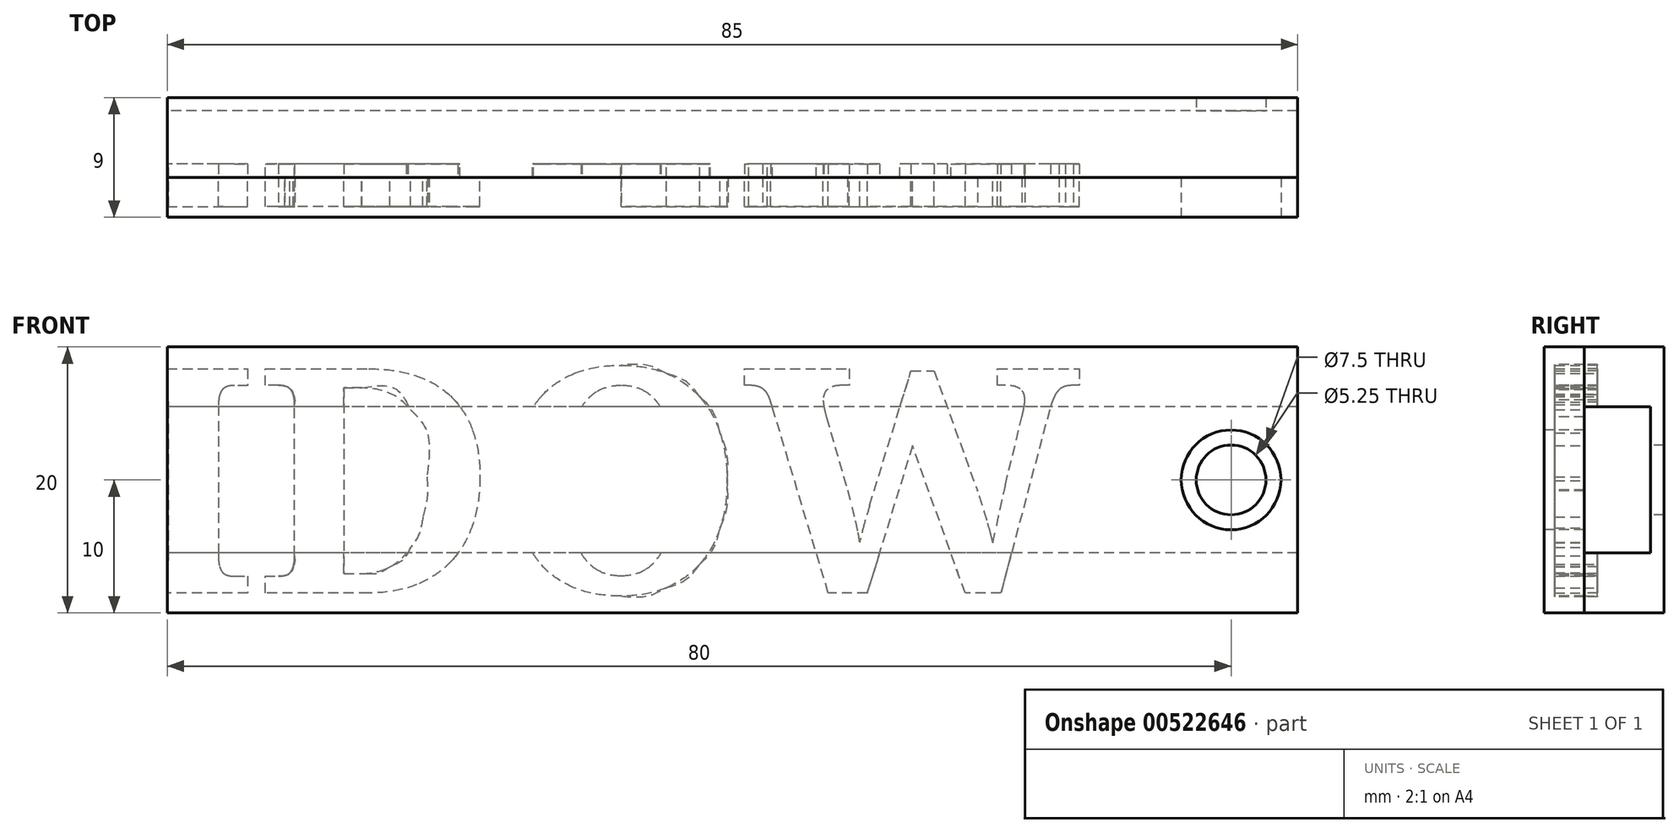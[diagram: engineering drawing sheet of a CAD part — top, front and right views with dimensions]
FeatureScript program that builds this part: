
annotation { "Feature Type Name" : "Feature", "Feature Type Description" : "" }
export const myFeature = defineFeature(function(context is Context, id is Id, definition is map)
    precondition{}
    {
        {
            var Q0;
            Q0=qCreatedBy(makeId("Front.planeOp"),FACE);
            var sketch = newSketch(context, id + "F0", { "sketchPlane" : qUnion([Q0])});
            skLineSegment(sketch, "E0.bottom", {"start": v(105, 10) * mm, "end": v(-105, 10) * mm});
            skLineSegment(sketch, "E0.top", {"start": v(105, -10) * mm, "end": v(-105, -10) * mm});
            skLineSegment(sketch, "E0.left", {"start": v(105, 10) * mm, "end": v(105, -10) * mm});
            skLineSegment(sketch, "E0.right", {"start": v(-105, 10) * mm, "end": v(-105, -10) * mm});
            skPoint(sketch, "E0.middle", {"position": v(0, 0) * mm});
            skSolve(sketch);
        }
        {
            var Q0;
            Q0 = qSketchRegion(id + "F0", true);
            extrude(context, id + "F1", {"entities" : qUnion([Q0]), "depth" : 1 * mm, "offsetDistance" : 25 * mm});
        }
        {
            var Q0;
            Q0=makeQuery(id+"F1.opExtrude","CAP_FACE",FACE,{"disambiguationData":[OSD([sQuery(id+"F0.wireOp",EDGE,"E0.bottom"),sQuery(id+"F0.wireOp",EDGE,"E0.top"),sQuery(id+"F0.wireOp",EDGE,"E0.left"),sQuery(id+"F0.wireOp",EDGE,"E0.right")])],"isStart":false});
            var sketch = newSketch(context, id + "F2", { "sketchPlane" : qUnion([Q0])});
            skText(sketch, "E1", { "text": "BLACKWIDOW", "fontName": "NotoSerif-Bold.ttf"});
            skLineSegment(sketch, "E2", {"start": v(0, 8.5) * mm, "end": v(0, -8.5) * mm, "construction": true});
            const initialGuessF2  = {"E1": [-0.09013, -0.0085, 1, 0, 0.017]};
            skSetInitialGuess(sketch, initialGuessF2);
            skSolve(sketch);
        }
        {
            var Q0;
            Q0 = qSketchRegion(id + "F2", true);
            var Q1;
            Q1=makeQuery(id+"F1.opExtrude","CAP_FACE",FACE,{"disambiguationData":[OSD([sQuery(id+"F0.wireOp",EDGE,"E0.bottom"),sQuery(id+"F0.wireOp",EDGE,"E0.top"),sQuery(id+"F0.wireOp",EDGE,"E0.left"),sQuery(id+"F0.wireOp",EDGE,"E0.right")])],"isStart":true});
            extrude(context, id + "F3", {"entities" : qUnion([Q0]), "operationType" : NewBodyOperationType.REMOVE, "endBound" : BoundingType.UP_TO_SURFACE, "oppositeDirection" : true, "depth" : 4 * mm, "endBoundEntityFace" : qUnion([Q1]), "offsetDistance" : 25 * mm});
        }
        {
            var Q0;
            {var subQ0=sQuery(id+"F0.wireOp",EDGE,"E0.left");var subQ1=sQuery(id+"F0.wireOp",EDGE,"E0.bottom");var subQ2=sQuery(id+"F0.wireOp",EDGE,"E0.right");var subQ3=sQuery(id+"F0.wireOp",EDGE,"E0.top");Q0=makeQuery(id+"F3.boolean.opBoolean","SPLIT",FACE,{"disambiguationData":[TD([makeQuery(id+"F1.opExtrude","SWEPT_FACE",FACE,{"disambiguationData":[OSD([subQ1])]})])],"derivedFrom":makeQuery(id+"F1.opExtrude","CAP_FACE",FACE,{"disambiguationData":[OSD([subQ1,subQ3,subQ0,subQ2])],"isStart":false})});}
            var sketch = newSketch(context, id + "F4", { "sketchPlane" : qUnion([Q0])});
            skLineSegment(sketch, "E3.bottom", {"start": v(-105, 10) * mm, "end": v(105, 10) * mm});
            skLineSegment(sketch, "E3.top", {"start": v(-105, -10) * mm, "end": v(105, -10) * mm});
            skLineSegment(sketch, "E3.left", {"start": v(-105, 10) * mm, "end": v(-105, -10) * mm});
            skLineSegment(sketch, "E3.right", {"start": v(105, 10) * mm, "end": v(105, -10) * mm});
            skSolve(sketch);
        }
        {
            var Q0;
            Q0 = qSketchRegion(id + "F4", true);
            extrude(context, id + "F5", {"entities" : qUnion([Q0]), "depth" : 3 * mm, "offsetDistance" : 25 * mm});
        }
        {
            var Q0;
            {var subQ0=sQuery(id+"F0.wireOp",EDGE,"E0.left");var subQ1=sQuery(id+"F0.wireOp",EDGE,"E0.bottom");var subQ2=sQuery(id+"F0.wireOp",EDGE,"E0.right");var subQ3=sQuery(id+"F0.wireOp",EDGE,"E0.top");Q0=makeQuery(id+"F3.boolean.opBoolean","SPLIT",FACE,{"disambiguationData":[TD([makeQuery(id+"F1.opExtrude","SWEPT_FACE",FACE,{"disambiguationData":[OSD([subQ1])]})])],"derivedFrom":makeQuery(id+"F1.opExtrude","CAP_FACE",FACE,{"disambiguationData":[OSD([subQ1,subQ3,subQ0,subQ2])],"isStart":true})});}
            var sketch = newSketch(context, id + "F6", { "sketchPlane" : qUnion([Q0])});
            skLineSegment(sketch, "E4.0", {"start": v(82.57, 8.36) * mm, "end": v(89.47, 8.36) * mm});
            skFitSpline(sketch, "E5.0", {"points": [v(75.82, 4.07) * mm, v(75.82, 6.28) * mm, v(77.51, 7.32) * mm]});
            skFitSpline(sketch, "E6.0", {"points": [v(77.51, 7.32) * mm, v(79.2, 8.36) * mm, v(82.57, 8.36) * mm]});
            skFitSpline(sketch, "E7.0", {"points": [v(76.03, 2.7) * mm, v(75.82, 3.28) * mm, v(75.82, 4.07) * mm]});
            skFitSpline(sketch, "E8.0", {"points": [v(76.64, 1.7) * mm, v(76.24, 2.12) * mm, v(76.03, 2.7) * mm]});
            skFitSpline(sketch, "E9.0", {"points": [v(78.8, 0.47) * mm, v(78.13, 0.68) * mm, v(77.58, 0.98) * mm]});
            skFitSpline(sketch, "E10.0", {"points": [v(77.58, 0.98) * mm, v(77.03, 1.28) * mm, v(76.64, 1.7) * mm]});
            skLineSegment(sketch, "E11.0", {"start": v(87.27, 5.6) * mm, "end": v(87.27, -5.71) * mm});
            skLineSegment(sketch, "E12.0", {"start": v(89.47, 7.1) * mm, "end": v(88.5, 7.1) * mm});
            skLineSegment(sketch, "E13.0.0", {"start": v(83.54, 6.91) * mm, "end": v(82.69, 6.91) * mm});
            skFitSpline(sketch, "E13.0.1", {"points": [v(82.69, 6.91) * mm, v(81.9, 6.91) * mm, v(81.34, 6.77) * mm]});
            skFitSpline(sketch, "E13.0.2", {"points": [v(81.34, 6.77) * mm, v(80.79, 6.63) * mm, v(80.44, 6.3) * mm]});
            skFitSpline(sketch, "E13.0.3", {"points": [v(80.44, 6.3) * mm, v(80.1, 5.96) * mm, v(79.94, 5.42) * mm]});
            skFitSpline(sketch, "E13.0.4", {"points": [v(79.94, 5.42) * mm, v(79.79, 4.87) * mm, v(79.79, 4.07) * mm]});
            skFitSpline(sketch, "E13.0.5", {"points": [v(79.79, 4.07) * mm, v(79.79, 3.26) * mm, v(79.92, 2.68) * mm]});
            skFitSpline(sketch, "E13.0.6", {"points": [v(79.92, 2.68) * mm, v(80.06, 2.1) * mm, v(80.4, 1.74) * mm]});
            skFitSpline(sketch, "E13.0.7", {"points": [v(80.4, 1.74) * mm, v(80.72, 1.38) * mm, v(81.27, 1.2) * mm]});
            skFitSpline(sketch, "E13.0.8", {"points": [v(81.27, 1.2) * mm, v(81.81, 1.03) * mm, v(82.64, 1.03) * mm]});
            skLineSegment(sketch, "E13.0.9", {"start": v(82.64, 1.03) * mm, "end": v(83.54, 1.03) * mm});
            skLineSegment(sketch, "E13.0.10", {"start": v(83.54, 1.03) * mm, "end": v(83.54, 6.91) * mm});
            skLineSegment(sketch, "E14.0.0", {"start": v(83.54, -0.4) * mm, "end": v(81.93, -0.4) * mm});
            skFitSpline(sketch, "E14.0.1", {"points": [v(81.93, -0.4) * mm, v(81.1, -0.4) * mm, v(80.57, -0.61) * mm]});
            skFitSpline(sketch, "E14.0.2", {"points": [v(80.57, -0.61) * mm, v(80.03, -0.82) * mm, v(79.7, -1.24) * mm]});
            skFitSpline(sketch, "E14.0.3", {"points": [v(79.7, -1.24) * mm, v(79.36, -1.65) * mm, v(79.22, -2.3) * mm]});
            skFitSpline(sketch, "E14.0.4", {"points": [v(79.22, -2.3) * mm, v(79.08, -2.93) * mm, v(79.08, -3.8) * mm]});
            skFitSpline(sketch, "E14.0.5", {"points": [v(79.08, -3.8) * mm, v(79.08, -4.7) * mm, v(79.24, -5.32) * mm]});
            skFitSpline(sketch, "E14.0.6", {"points": [v(79.24, -5.32) * mm, v(79.4, -5.94) * mm, v(79.74, -6.33) * mm]});
            skFitSpline(sketch, "E14.0.7", {"points": [v(79.74, -6.33) * mm, v(80.08, -6.71) * mm, v(80.64, -6.89) * mm]});
            skFitSpline(sketch, "E14.0.8", {"points": [v(80.64, -6.89) * mm, v(81.2, -7.06) * mm, v(81.98, -7.06) * mm]});
            skLineSegment(sketch, "E14.0.9", {"start": v(81.98, -7.06) * mm, "end": v(83.54, -7.06) * mm});
            skLineSegment(sketch, "E14.0.10", {"start": v(83.54, -7.06) * mm, "end": v(83.54, -0.4) * mm});
            skFitSpline(sketch, "E15.0", {"points": [v(87.36, 6.37) * mm, v(87.27, 6.07) * mm, v(87.27, 5.6) * mm]});
            skFitSpline(sketch, "E16.0", {"points": [v(87.63, 6.82) * mm, v(87.46, 6.66) * mm, v(87.36, 6.37) * mm]});
            skFitSpline(sketch, "E17.0", {"points": [v(88.02, 7.05) * mm, v(87.8, 6.98) * mm, v(87.63, 6.82) * mm]});
            skFitSpline(sketch, "E18.0", {"points": [v(88.5, 7.1) * mm, v(88.25, 7.1) * mm, v(88.02, 7.05) * mm]});
            skFitSpline(sketch, "E19.0", {"points": [v(81.86, -8.5) * mm, v(78.5, -8.5) * mm, v(76.8, -7.35) * mm]});
            skFitSpline(sketch, "E20.0", {"points": [v(76.8, -7.35) * mm, v(75.1, -6.2) * mm, v(75.1, -3.88) * mm]});
            skFitSpline(sketch, "E21.0", {"points": [v(75.1, -3.88) * mm, v(75.1, -3.01) * mm, v(75.37, -2.32) * mm]});
            skFitSpline(sketch, "E22.0", {"points": [v(75.37, -2.32) * mm, v(75.65, -1.63) * mm, v(76.14, -1.1) * mm]});
            skFitSpline(sketch, "E23.0", {"points": [v(76.14, -1.1) * mm, v(76.63, -0.58) * mm, v(77.3, -0.22) * mm]});
            skFitSpline(sketch, "E24.0", {"points": [v(77.3, -0.22) * mm, v(77.97, 0.15) * mm, v(78.8, 0.35) * mm]});
            skLineSegment(sketch, "E25.0", {"start": v(78.8, 0.35) * mm, "end": v(78.8, 0.47) * mm});
            skLineSegment(sketch, "E26.0", {"start": v(89.47, -8.5) * mm, "end": v(81.86, -8.5) * mm});
            skLineSegment(sketch, "E27.0", {"start": v(89.47, -7.24) * mm, "end": v(89.47, -8.5) * mm});
            skLineSegment(sketch, "E28.0", {"start": v(88.5, -7.24) * mm, "end": v(89.47, -7.24) * mm});
            skFitSpline(sketch, "E29.0", {"points": [v(87.62, -6.98) * mm, v(87.79, -7.14) * mm, v(88.01, -7.2) * mm]});
            skFitSpline(sketch, "E30.0", {"points": [v(88.01, -7.2) * mm, v(88.23, -7.24) * mm, v(88.5, -7.24) * mm]});
            skFitSpline(sketch, "E31.0", {"points": [v(87.36, -6.52) * mm, v(87.46, -6.82) * mm, v(87.62, -6.98) * mm]});
            skFitSpline(sketch, "E32.0", {"points": [v(87.27, -5.71) * mm, v(87.27, -6.22) * mm, v(87.36, -6.52) * mm]});
            skLineSegment(sketch, "E33.0", {"start": v(67.66, -7.06) * mm, "end": v(67.66, 5.67) * mm});
            skLineSegment(sketch, "E34.0", {"start": v(73.6, 7.1) * mm, "end": v(72.61, 7.1) * mm});
            skLineSegment(sketch, "E35.0", {"start": v(73.6, 8.36) * mm, "end": v(73.6, 7.1) * mm});
            skLineSegment(sketch, "E36.0", {"start": v(65.45, 8.36) * mm, "end": v(73.6, 8.36) * mm});
            skFitSpline(sketch, "E37.0", {"points": [v(71.5, 6.38) * mm, v(71.4, 6.08) * mm, v(71.4, 5.58) * mm]});
            skFitSpline(sketch, "E38.0", {"points": [v(71.75, 6.85) * mm, v(71.59, 6.68) * mm, v(71.5, 6.38) * mm]});
            skFitSpline(sketch, "E39.0", {"points": [v(72.13, 7.06) * mm, v(71.9, 7) * mm, v(71.75, 6.85) * mm]});
            skFitSpline(sketch, "E40.0", {"points": [v(72.61, 7.1) * mm, v(72.35, 7.1) * mm, v(72.13, 7.06) * mm]});
            skLineSegment(sketch, "E41.0", {"start": v(71.4, 5.58) * mm, "end": v(71.4, -5.71) * mm});
            skLineSegment(sketch, "E42.0", {"start": v(65.45, 7.1) * mm, "end": v(65.45, 8.36) * mm});
            skLineSegment(sketch, "E43.0", {"start": v(66.44, 7.1) * mm, "end": v(65.45, 7.1) * mm});
            skFitSpline(sketch, "E44.0", {"points": [v(66.91, 7.06) * mm, v(66.69, 7.1) * mm, v(66.44, 7.1) * mm]});
            skFitSpline(sketch, "E45.0", {"points": [v(67.3, 6.86) * mm, v(67.14, 7) * mm, v(66.91, 7.06) * mm]});
            skFitSpline(sketch, "E46.0", {"points": [v(67.56, 6.42) * mm, v(67.46, 6.7) * mm, v(67.3, 6.86) * mm]});
            skFitSpline(sketch, "E47.0", {"points": [v(67.66, 5.67) * mm, v(67.66, 6.14) * mm, v(67.56, 6.42) * mm]});
            skLineSegment(sketch, "E48.0", {"start": v(59.77, -8.5) * mm, "end": v(59.6, -3.23) * mm});
            skLineSegment(sketch, "E49.0", {"start": v(59.6, -3.23) * mm, "end": v(60.92, -3.23) * mm});
            skLineSegment(sketch, "E50.0", {"start": v(60.92, -3.23) * mm, "end": v(61.3, -5) * mm});
            skFitSpline(sketch, "E51.0", {"points": [v(61.3, -5) * mm, v(61.51, -6) * mm, v(61.97, -6.53) * mm]});
            skFitSpline(sketch, "E52.0", {"points": [v(61.97, -6.53) * mm, v(62.43, -7.06) * mm, v(63.26, -7.06) * mm]});
            skLineSegment(sketch, "E53.0", {"start": v(63.26, -7.06) * mm, "end": v(67.66, -7.06) * mm});
            skLineSegment(sketch, "E54.0", {"start": v(73.6, -8.5) * mm, "end": v(59.77, -8.5) * mm});
            skLineSegment(sketch, "E55.0", {"start": v(73.6, -7.24) * mm, "end": v(73.6, -8.5) * mm});
            skLineSegment(sketch, "E56.0", {"start": v(72.61, -7.24) * mm, "end": v(73.6, -7.24) * mm});
            skFitSpline(sketch, "E57.0", {"points": [v(71.4, -5.71) * mm, v(71.4, -6.22) * mm, v(71.5, -6.52) * mm]});
            skFitSpline(sketch, "E58.0", {"points": [v(71.5, -6.52) * mm, v(71.59, -6.82) * mm, v(71.75, -6.98) * mm]});
            skFitSpline(sketch, "E59.0", {"points": [v(72.13, -7.2) * mm, v(72.35, -7.24) * mm, v(72.61, -7.24) * mm]});
            skFitSpline(sketch, "E60.0", {"points": [v(71.75, -6.98) * mm, v(71.9, -7.14) * mm, v(72.13, -7.2) * mm]});
            skLineSegment(sketch, "E61.0", {"start": v(43.26, -5.55) * mm, "end": v(48.2, 8.36) * mm});
            skFitSpline(sketch, "E61.1", {"points": [v(42.9, -6.37) * mm, v(43.09, -6.04) * mm, v(43.26, -5.55) * mm]});
            skFitSpline(sketch, "E61.2", {"points": [v(42.48, -6.9) * mm, v(42.7, -6.7) * mm, v(42.9, -6.37) * mm]});
            skLineSegment(sketch, "E62.0", {"start": v(41.05, -8.5) * mm, "end": v(41.05, -7.24) * mm});
            skFitSpline(sketch, "E62.1", {"points": [v(42, -7.16) * mm, v(42.26, -7.08) * mm, v(42.48, -6.9) * mm]});
            skFitSpline(sketch, "E62.2", {"points": [v(41.48, -7.24) * mm, v(41.75, -7.24) * mm, v(42, -7.16) * mm]});
            skLineSegment(sketch, "E62.3", {"start": v(41.05, -7.24) * mm, "end": v(41.48, -7.24) * mm});
            skLineSegment(sketch, "E62.4", {"start": v(48.84, -8.5) * mm, "end": v(41.05, -8.5) * mm});
            skLineSegment(sketch, "E62.5", {"start": v(48.84, -7.24) * mm, "end": v(48.84, -8.5) * mm});
            skLineSegment(sketch, "E62.6", {"start": v(47.92, -7.24) * mm, "end": v(48.84, -7.24) * mm});
            skFitSpline(sketch, "E62.7", {"points": [v(47.24, -7.03) * mm, v(47.38, -7.14) * mm, v(47.56, -7.2) * mm]});
            skFitSpline(sketch, "E62.8", {"points": [v(47.56, -7.2) * mm, v(47.75, -7.24) * mm, v(47.92, -7.24) * mm]});
            skFitSpline(sketch, "E62.9", {"points": [v(47, -6.75) * mm, v(47.1, -6.92) * mm, v(47.24, -7.03) * mm]});
            skLineSegment(sketch, "E62.10", {"start": v(47.94, -2.96) * mm, "end": v(47.11, -5.32) * mm});
            skLineSegment(sketch, "E62.11", {"start": v(53.68, -2.96) * mm, "end": v(47.94, -2.96) * mm});
            skLineSegment(sketch, "E62.12", {"start": v(54.37, -4.98) * mm, "end": v(53.68, -2.96) * mm});
            skLineSegment(sketch, "E62.13", {"start": v(52.59, -8.5) * mm, "end": v(52.59, -7.24) * mm});
            skFitSpline(sketch, "E62.14", {"points": [v(54.56, -5.66) * mm, v(54.46, -5.27) * mm, v(54.37, -4.98) * mm]});
            skFitSpline(sketch, "E62.15", {"points": [v(54.65, -6.33) * mm, v(54.65, -6.04) * mm, v(54.56, -5.66) * mm]});
            skFitSpline(sketch, "E62.16", {"points": [v(54.56, -6.74) * mm, v(54.65, -6.56) * mm, v(54.65, -6.33) * mm]});
            skLineSegment(sketch, "E62.17", {"start": v(52.59, -7.24) * mm, "end": v(53.58, -7.24) * mm});
            skFitSpline(sketch, "E62.18", {"points": [v(53.58, -7.24) * mm, v(53.79, -7.24) * mm, v(53.98, -7.18) * mm]});
            skFitSpline(sketch, "E62.19", {"points": [v(53.98, -7.18) * mm, v(54.17, -7.13) * mm, v(54.32, -7.02) * mm]});
            skFitSpline(sketch, "E62.20", {"points": [v(54.32, -7.02) * mm, v(54.47, -6.9) * mm, v(54.56, -6.74) * mm]});
            skLineSegment(sketch, "E62.21", {"start": v(51.44, 8.36) * mm, "end": v(56.55, -5.53) * mm});
            skLineSegment(sketch, "E63.0", {"start": v(53.19, -1.51) * mm, "end": v(51.8, 2.48) * mm});
            skLineSegment(sketch, "E63.1", {"start": v(49.66, 2.36) * mm, "end": v(48.42, -1.51) * mm});
            skFitSpline(sketch, "E63.2", {"points": [v(49.92, 3.2) * mm, v(49.79, 2.76) * mm, v(49.66, 2.36) * mm]});
            skFitSpline(sketch, "E63.3", {"points": [v(50.19, 4.11) * mm, v(50.05, 3.65) * mm, v(49.92, 3.2) * mm]});
            skFitSpline(sketch, "E63.4", {"points": [v(50.44, 5.03) * mm, v(50.32, 4.57) * mm, v(50.19, 4.11) * mm]});
            skFitSpline(sketch, "E63.5", {"points": [v(51.19, 4.24) * mm, v(51.03, 4.69) * mm, v(50.9, 5.12) * mm]});
            skFitSpline(sketch, "E63.6", {"points": [v(51.5, 3.34) * mm, v(51.34, 3.79) * mm, v(51.19, 4.24) * mm]});
            skFitSpline(sketch, "E63.7", {"points": [v(51.8, 2.48) * mm, v(51.65, 2.9) * mm, v(51.5, 3.34) * mm]});
            skLineSegment(sketch, "E63.8", {"start": v(48.42, -1.51) * mm, "end": v(53.19, -1.51) * mm});
            skFitSpline(sketch, "E63.9", {"points": [v(50.9, 5.12) * mm, v(50.75, 5.54) * mm, v(50.65, 5.9) * mm]});
            skFitSpline(sketch, "E63.10", {"points": [v(50.65, 5.9) * mm, v(50.56, 5.49) * mm, v(50.44, 5.03) * mm]});
            skLineSegment(sketch, "E63.11", {"start": v(48.2, 8.36) * mm, "end": v(51.44, 8.36) * mm});
            skFitSpline(sketch, "E63.12", {"points": [v(56.55, -5.53) * mm, v(56.76, -6.05) * mm, v(56.97, -6.39) * mm]});
            skFitSpline(sketch, "E63.13", {"points": [v(56.97, -6.39) * mm, v(57.17, -6.73) * mm, v(57.4, -6.92) * mm]});
            skFitSpline(sketch, "E63.14", {"points": [v(57.4, -6.92) * mm, v(57.62, -7.1) * mm, v(57.87, -7.17) * mm]});
            skFitSpline(sketch, "E63.15", {"points": [v(57.87, -7.17) * mm, v(58.13, -7.24) * mm, v(58.45, -7.24) * mm]});
            skLineSegment(sketch, "E63.16", {"start": v(58.45, -7.24) * mm, "end": v(58.73, -7.24) * mm});
            skLineSegment(sketch, "E63.17", {"start": v(58.73, -7.24) * mm, "end": v(58.73, -8.5) * mm});
            skLineSegment(sketch, "E63.18", {"start": v(58.73, -8.5) * mm, "end": v(52.59, -8.5) * mm});
            skLineSegment(sketch, "E64.0", {"start": v(-29.57, 5.67) * mm, "end": v(-29.57, -5.71) * mm});
            skFitSpline(sketch, "E65.0", {"points": [v(-38.67, 7.84) * mm, v(-37.12, 8.36) * mm, v(-35.16, 8.36) * mm]});
            skLineSegment(sketch, "E66.0", {"start": v(-35.16, 8.36) * mm, "end": v(-27.36, 8.36) * mm});
            skLineSegment(sketch, "E67.0", {"start": v(-27.36, 7.1) * mm, "end": v(-28.36, 7.1) * mm});
            skFitSpline(sketch, "E68.0", {"points": [v(-29.22, 6.86) * mm, v(-29.38, 6.7) * mm, v(-29.48, 6.42) * mm]});
            skFitSpline(sketch, "E69.0", {"points": [v(-29.48, 6.42) * mm, v(-29.57, 6.14) * mm, v(-29.57, 5.67) * mm]});
            skPoint(sketch, "E70.0", {"position": v(-28.6, 7.1) * mm});
            skLineSegment(sketch, "E71.0", {"start": v(-27.36, 8.36) * mm, "end": v(-27.36, 7.1) * mm});
            skFitSpline(sketch, "E72.0", {"points": [v(-29.48, 6.42) * mm, v(-29.57, 6.14) * mm, v(-29.57, 5.67) * mm]});
            skLineSegment(sketch, "E73.0", {"start": v(-33.29, -7.04) * mm, "end": v(-33.29, 6.91) * mm});
            skLineSegment(sketch, "E74.0", {"start": v(-33.29, 6.91) * mm, "end": v(-34.64, 6.91) * mm});
            skFitSpline(sketch, "E75.0", {"points": [v(-34.64, 6.91) * mm, v(-37.05, 6.91) * mm, v(-38.29, 5.26) * mm]});
            skFitSpline(sketch, "E76.0", {"points": [v(-38.29, 5.26) * mm, v(-39.53, 3.62) * mm, v(-39.53, 0.24) * mm]});
            skFitSpline(sketch, "E77.0", {"points": [v(-39.53, 0.24) * mm, v(-39.53, -1.46) * mm, v(-39.22, -2.8) * mm]});
            skFitSpline(sketch, "E78.0", {"points": [v(-39.22, -2.8) * mm, v(-38.9, -4.14) * mm, v(-38.29, -5.09) * mm]});
            skFitSpline(sketch, "E79.0", {"points": [v(-38.29, -5.09) * mm, v(-37.67, -6.03) * mm, v(-36.75, -6.53) * mm]});
            skFitSpline(sketch, "E80.0", {"points": [v(-36.75, -6.53) * mm, v(-35.83, -7.04) * mm, v(-34.62, -7.04) * mm]});
            skLineSegment(sketch, "E81.0", {"start": v(-34.62, -7.04) * mm, "end": v(-33.29, -7.04) * mm});
            skFitSpline(sketch, "E82.0", {"points": [v(-41.3, 6.31) * mm, v(-40.22, 7.33) * mm, v(-38.67, 7.84) * mm]});
            skFitSpline(sketch, "E83.0", {"points": [v(-42.95, 3.77) * mm, v(-42.38, 5.3) * mm, v(-41.3, 6.31) * mm]});
            skFitSpline(sketch, "E84.0", {"points": [v(-43.52, 0.24) * mm, v(-43.52, 2.25) * mm, v(-42.95, 3.77) * mm]});
            skFitSpline(sketch, "E85.0", {"points": [v(-42.99, -3.3) * mm, v(-43.52, -1.7) * mm, v(-43.52, 0.24) * mm]});
            skFitSpline(sketch, "E86.0", {"points": [v(-41.4, -6.07) * mm, v(-42.46, -4.91) * mm, v(-42.99, -3.3) * mm]});
            skPoint(sketch, "E87.0", {"position": v(-40.2, -7.1) * mm});
            skFitSpline(sketch, "E88.0", {"points": [v(-35.16, -8.5) * mm, v(-37.22, -8.5) * mm, v(-38.78, -7.86) * mm]});
            skLineSegment(sketch, "E89.0", {"start": v(-27.36, -8.5) * mm, "end": v(-35.16, -8.5) * mm});
            skLineSegment(sketch, "E90.0", {"start": v(-27.36, -7.24) * mm, "end": v(-27.36, -8.5) * mm});
            skLineSegment(sketch, "E91.0", {"start": v(-28.36, -7.24) * mm, "end": v(-27.36, -7.24) * mm});
            skPoint(sketch, "E92.0", {"position": v(-28.6, -7.23) * mm});
            skFitSpline(sketch, "E93.0", {"points": [v(-29.57, -5.71) * mm, v(-29.57, -6.22) * mm, v(-29.48, -6.52) * mm]});
            skFitSpline(sketch, "E94.0", {"points": [v(-29.48, -6.52) * mm, v(-29.38, -6.82) * mm, v(-29.22, -6.98) * mm]});
            skFitSpline(sketch, "E95.0", {"points": [v(-28.36, 7.1) * mm, v(-28.61, 7.1) * mm, v(-28.83, 7.06) * mm]});
            skFitSpline(sketch, "E96.0", {"points": [v(-28.83, 7.06) * mm, v(-29.05, 7) * mm, v(-29.22, 6.86) * mm]});
            skFitSpline(sketch, "E97.0", {"points": [v(-38.78, -7.86) * mm, v(-40.35, -7.22) * mm, v(-41.4, -6.07) * mm]});
            skFitSpline(sketch, "E98.0", {"points": [v(-35.16, -8.5) * mm, v(-37.22, -8.5) * mm, v(-38.78, -7.86) * mm]});
            skFitSpline(sketch, "E99.0", {"points": [v(-29.48, -6.52) * mm, v(-29.38, -6.82) * mm, v(-29.22, -6.98) * mm]});
            skFitSpline(sketch, "E100.0", {"points": [v(-29.57, -5.71) * mm, v(-29.57, -6.22) * mm, v(-29.48, -6.52) * mm]});
            skFitSpline(sketch, "E101.0", {"points": [v(-29.48, -6.52) * mm, v(-29.38, -6.82) * mm, v(-29.22, -6.98) * mm]});
            skFitSpline(sketch, "E102.0", {"points": [v(-28.84, -7.2) * mm, v(-28.62, -7.24) * mm, v(-28.36, -7.24) * mm]});
            skFitSpline(sketch, "E103.0", {"points": [v(-29.22, -6.98) * mm, v(-29.06, -7.14) * mm, v(-28.84, -7.2) * mm]});
            skFitSpline(sketch, "E104.0", {"points": [v(-29.22, -6.98) * mm, v(-29.06, -7.14) * mm, v(-28.84, -7.2) * mm]});
            skFitSpline(sketch, "E105.0", {"points": [v(-28.84, -7.2) * mm, v(-28.62, -7.24) * mm, v(-28.36, -7.24) * mm]});
            skFitSpline(sketch, "E106.0", {"points": [v(35.78, -0.05) * mm, v(35.78, 1.66) * mm, v(35.57, 2.99) * mm]});
            skFitSpline(sketch, "E107.0", {"points": [v(35.53, -3.04) * mm, v(35.78, -1.76) * mm, v(35.78, -0.05) * mm]});
            skFitSpline(sketch, "E108.0", {"points": [v(39.75, -0.05) * mm, v(39.75, -2) * mm, v(39.24, -3.6) * mm]});
            skFitSpline(sketch, "E108.1", {"points": [v(39.23, 3.45) * mm, v(39.75, 1.86) * mm, v(39.75, -0.05) * mm]});
            skFitSpline(sketch, "E108.2", {"points": [v(37.72, -6.34) * mm, v(36.7, -7.49) * mm, v(35.17, -8.1) * mm]});
            skFitSpline(sketch, "E108.3", {"points": [v(35.17, -8.1) * mm, v(33.64, -8.73) * mm, v(31.58, -8.73) * mm]});
            skFitSpline(sketch, "E108.4", {"points": [v(31.58, -8.73) * mm, v(30.07, -8.73) * mm, v(29.05, -8.43) * mm]});
            skFitSpline(sketch, "E108.5", {"points": [v(29.05, -8.43) * mm, v(28.02, -8.13) * mm, v(27.4, -7.67) * mm]});
            skFitSpline(sketch, "E108.6", {"points": [v(27.4, -7.67) * mm, v(26.77, -7.2) * mm, v(26.5, -6.66) * mm]});
            skFitSpline(sketch, "E108.7", {"points": [v(26.5, -6.66) * mm, v(26.24, -6.11) * mm, v(26.24, -5.62) * mm]});
            skFitSpline(sketch, "E108.8", {"points": [v(34.7, -5.16) * mm, v(35.27, -4.32) * mm, v(35.53, -3.04) * mm]});
            skFitSpline(sketch, "E108.9", {"points": [v(33.24, -6.43) * mm, v(34.14, -6) * mm, v(34.7, -5.16) * mm]});
            skFitSpline(sketch, "E108.10", {"points": [v(31.02, -6.85) * mm, v(32.33, -6.85) * mm, v(33.24, -6.43) * mm]});
            skFitSpline(sketch, "E108.11", {"points": [v(29.48, -6.65) * mm, v(30.15, -6.85) * mm, v(31.02, -6.85) * mm]});
            skFitSpline(sketch, "E108.12", {"points": [v(28.27, -6.13) * mm, v(28.8, -6.45) * mm, v(29.48, -6.65) * mm]});
            skFitSpline(sketch, "E108.13", {"points": [v(27.35, -5.4) * mm, v(27.74, -5.8) * mm, v(28.27, -6.13) * mm]});
            skFitSpline(sketch, "E108.14", {"points": [v(26.65, -4.6) * mm, v(26.95, -5) * mm, v(27.35, -5.4) * mm]});
            skFitSpline(sketch, "E108.15", {"points": [v(26.35, -5.03) * mm, v(26.46, -4.74) * mm, v(26.65, -4.6) * mm]});
            skFitSpline(sketch, "E108.16", {"points": [v(26.24, -5.62) * mm, v(26.24, -5.32) * mm, v(26.35, -5.03) * mm]});
            skFitSpline(sketch, "E108.17", {"points": [v(39.24, -3.6) * mm, v(38.73, -5.2) * mm, v(37.72, -6.34) * mm]});
            skFitSpline(sketch, "E108.18", {"points": [v(37.69, 6.19) * mm, v(38.7, 5.05) * mm, v(39.23, 3.45) * mm]});
            skFitSpline(sketch, "E108.19", {"points": [v(35.14, 7.96) * mm, v(36.67, 7.33) * mm, v(37.69, 6.19) * mm]});
            skFitSpline(sketch, "E108.20", {"points": [v(31.6, 8.6) * mm, v(33.61, 8.6) * mm, v(35.14, 7.96) * mm]});
            skFitSpline(sketch, "E108.21", {"points": [v(29.24, 8.38) * mm, v(30.25, 8.6) * mm, v(31.6, 8.6) * mm]});
            skFitSpline(sketch, "E108.22", {"points": [v(27.56, 7.8) * mm, v(28.23, 8.17) * mm, v(29.24, 8.38) * mm]});
            skFitSpline(sketch, "E108.23", {"points": [v(26.56, 6.93) * mm, v(26.89, 7.43) * mm, v(27.56, 7.8) * mm]});
            skFitSpline(sketch, "E108.24", {"points": [v(26.22, 5.85) * mm, v(26.22, 6.43) * mm, v(26.56, 6.93) * mm]});
            skFitSpline(sketch, "E108.25", {"points": [v(26.41, 5.04) * mm, v(26.22, 5.42) * mm, v(26.22, 5.85) * mm]});
            skFitSpline(sketch, "E108.26", {"points": [v(26.98, 4.4) * mm, v(26.6, 4.67) * mm, v(26.41, 5.04) * mm]});
            skFitSpline(sketch, "E108.27", {"points": [v(27.9, 3.96) * mm, v(27.35, 4.11) * mm, v(26.98, 4.4) * mm]});
            skFitSpline(sketch, "E108.28", {"points": [v(29.17, 3.8) * mm, v(28.46, 3.8) * mm, v(27.9, 3.96) * mm]});
            skFitSpline(sketch, "E108.29", {"points": [v(29.3, 4.97) * mm, v(29.17, 4.4) * mm, v(29.17, 3.8) * mm]});
            skFitSpline(sketch, "E108.30", {"points": [v(29.73, 6.03) * mm, v(29.43, 5.55) * mm, v(29.3, 4.97) * mm]});
            skFitSpline(sketch, "E108.31", {"points": [v(30.53, 6.8) * mm, v(30.04, 6.5) * mm, v(29.73, 6.03) * mm]});
            skFitSpline(sketch, "E108.32", {"points": [v(35.57, 2.99) * mm, v(35.36, 4.32) * mm, v(34.9, 5.23) * mm]});
            skFitSpline(sketch, "E108.33", {"points": [v(34.9, 5.23) * mm, v(34.43, 6.14) * mm, v(33.66, 6.61) * mm]});
            skFitSpline(sketch, "E108.34", {"points": [v(33.66, 6.61) * mm, v(32.88, 7.09) * mm, v(31.77, 7.09) * mm]});
            skFitSpline(sketch, "E108.35", {"points": [v(31.77, 7.09) * mm, v(31.03, 7.09) * mm, v(30.53, 6.8) * mm]});
            skPoint(sketch, "E108.36", {"position": v(38.62, -5.05) * mm});
            skLineSegment(sketch, "E109.0", {"start": v(22.42, 5.67) * mm, "end": v(22.42, -5.84) * mm});
            skFitSpline(sketch, "E110.0", {"points": [v(22.5, 6.42) * mm, v(22.42, 6.14) * mm, v(22.42, 5.67) * mm]});
            skFitSpline(sketch, "E110.1", {"points": [v(22.77, 6.86) * mm, v(22.6, 6.7) * mm, v(22.5, 6.42) * mm]});
            skLineSegment(sketch, "E110.2", {"start": v(16.47, 8.36) * mm, "end": v(24.62, 8.36) * mm});
            skLineSegment(sketch, "E110.3", {"start": v(24.62, 8.36) * mm, "end": v(24.62, 7.1) * mm});
            skLineSegment(sketch, "E110.4", {"start": v(24.62, 7.1) * mm, "end": v(23.63, 7.1) * mm});
            skFitSpline(sketch, "E110.5", {"points": [v(23.16, 7.06) * mm, v(22.94, 7) * mm, v(22.77, 6.86) * mm]});
            skFitSpline(sketch, "E110.6", {"points": [v(23.63, 7.1) * mm, v(23.37, 7.1) * mm, v(23.16, 7.06) * mm]});
            skLineSegment(sketch, "E110.7", {"start": v(16.47, 7.1) * mm, "end": v(16.47, 8.36) * mm});
            skLineSegment(sketch, "E110.8", {"start": v(17.46, 7.1) * mm, "end": v(16.47, 7.1) * mm});
            skFitSpline(sketch, "E110.9", {"points": [v(17.94, 7.06) * mm, v(17.71, 7.1) * mm, v(17.46, 7.1) * mm]});
            skLineSegment(sketch, "E110.10", {"start": v(18.7, 0.07) * mm, "end": v(18.7, 5.58) * mm});
            skFitSpline(sketch, "E110.11", {"points": [v(18.7, 5.58) * mm, v(18.7, 6.08) * mm, v(18.6, 6.38) * mm]});
            skFitSpline(sketch, "E110.12", {"points": [v(18.6, 6.38) * mm, v(18.5, 6.68) * mm, v(18.34, 6.85) * mm]});
            skFitSpline(sketch, "E110.13", {"points": [v(18.34, 6.85) * mm, v(18.18, 7) * mm, v(17.94, 7.06) * mm]});
            skLineSegment(sketch, "E110.14", {"start": v(15.03, 4.07) * mm, "end": v(18.7, 0.07) * mm});
            skFitSpline(sketch, "E110.15", {"points": [v(14.39, 4.8) * mm, v(14.65, 4.47) * mm, v(15.03, 4.07) * mm]});
            skFitSpline(sketch, "E110.16", {"points": [v(13.75, 5.95) * mm, v(13.82, 5.7) * mm, v(13.97, 5.41) * mm]});
            skFitSpline(sketch, "E110.17", {"points": [v(13.68, 6.44) * mm, v(13.68, 6.2) * mm, v(13.75, 5.95) * mm]});
            skFitSpline(sketch, "E110.18", {"points": [v(13.98, 6.98) * mm, v(13.68, 6.83) * mm, v(13.68, 6.44) * mm]});
            skFitSpline(sketch, "E110.19", {"points": [v(15, 7.13) * mm, v(14.28, 7.13) * mm, v(13.98, 6.98) * mm]});
            skLineSegment(sketch, "E110.20", {"start": v(15, 8.36) * mm, "end": v(15, 7.13) * mm});
            skLineSegment(sketch, "E110.21", {"start": v(8.6, 8.36) * mm, "end": v(15, 8.36) * mm});
            skLineSegment(sketch, "E110.22", {"start": v(8.6, 7.13) * mm, "end": v(8.6, 8.36) * mm});
            skFitSpline(sketch, "E110.23", {"points": [v(9.52, 6.98) * mm, v(9.09, 7.13) * mm, v(8.6, 7.13) * mm]});
            skFitSpline(sketch, "E110.24", {"points": [v(10.37, 6.56) * mm, v(9.96, 6.83) * mm, v(9.52, 6.98) * mm]});
            skFitSpline(sketch, "E110.25", {"points": [v(11.19, 5.9) * mm, v(10.79, 6.28) * mm, v(10.37, 6.56) * mm]});
            skFitSpline(sketch, "E110.26", {"points": [v(12, 5.06) * mm, v(11.6, 5.52) * mm, v(11.19, 5.9) * mm]});
            skLineSegment(sketch, "E110.27", {"start": v(15.12, 1.63) * mm, "end": v(12, 5.06) * mm});
            skLineSegment(sketch, "E110.28", {"start": v(10.73, -5.34) * mm, "end": v(15.12, 1.63) * mm});
            skLineSegment(sketch, "E110.29", {"start": v(18.7, -5.71) * mm, "end": v(18.7, -1.72) * mm});
            skLineSegment(sketch, "E110.30", {"start": v(18.7, -1.72) * mm, "end": v(17.64, -0.9) * mm});
            skLineSegment(sketch, "E110.31", {"start": v(17.64, -0.9) * mm, "end": v(14.46, -6.33) * mm});
            skFitSpline(sketch, "E110.32", {"points": [v(22.42, -5.84) * mm, v(22.42, -6.3) * mm, v(22.5, -6.58) * mm]});
            skLineSegment(sketch, "E110.33", {"start": v(24.62, -7.24) * mm, "end": v(24.62, -8.5) * mm});
            skLineSegment(sketch, "E110.34", {"start": v(24.62, -8.5) * mm, "end": v(16.47, -8.5) * mm});
            skLineSegment(sketch, "E110.35", {"start": v(16.47, -8.5) * mm, "end": v(16.47, -7.24) * mm});
            skLineSegment(sketch, "E110.36", {"start": v(16.47, -7.24) * mm, "end": v(17.46, -7.24) * mm});
            skFitSpline(sketch, "E110.37", {"points": [v(17.46, -7.24) * mm, v(17.71, -7.24) * mm, v(17.94, -7.2) * mm]});
            skFitSpline(sketch, "E110.38", {"points": [v(17.94, -7.2) * mm, v(18.18, -7.14) * mm, v(18.34, -6.98) * mm]});
            skFitSpline(sketch, "E110.39", {"points": [v(18.34, -6.98) * mm, v(18.5, -6.82) * mm, v(18.6, -6.52) * mm]});
            skFitSpline(sketch, "E110.40", {"points": [v(18.6, -6.52) * mm, v(18.7, -6.22) * mm, v(18.7, -5.71) * mm]});
            skLineSegment(sketch, "E110.41", {"start": v(23.63, -7.24) * mm, "end": v(24.62, -7.24) * mm});
            skFitSpline(sketch, "E110.42", {"points": [v(23.16, -7.2) * mm, v(23.37, -7.24) * mm, v(23.63, -7.24) * mm]});
            skFitSpline(sketch, "E110.43", {"points": [v(22.77, -7) * mm, v(22.94, -7.15) * mm, v(23.16, -7.2) * mm]});
            skFitSpline(sketch, "E110.44", {"points": [v(22.5, -6.58) * mm, v(22.6, -6.86) * mm, v(22.77, -7) * mm]});
            skFitSpline(sketch, "E110.45", {"points": [v(10.06, -6.26) * mm, v(10.38, -5.9) * mm, v(10.73, -5.34) * mm]});
            skFitSpline(sketch, "E110.46", {"points": [v(9.43, -6.84) * mm, v(9.75, -6.62) * mm, v(10.06, -6.26) * mm]});
            skFitSpline(sketch, "E110.47", {"points": [v(8.77, -7.15) * mm, v(9.1, -7.06) * mm, v(9.43, -6.84) * mm]});
            skFitSpline(sketch, "E110.48", {"points": [v(8.04, -7.24) * mm, v(8.43, -7.24) * mm, v(8.77, -7.15) * mm]});
            skLineSegment(sketch, "E110.49", {"start": v(7.95, -8.5) * mm, "end": v(7.95, -7.24) * mm});
            skLineSegment(sketch, "E110.50", {"start": v(9.22, -8.5) * mm, "end": v(7.95, -8.5) * mm});
            skFitSpline(sketch, "E110.51", {"points": [v(10.8, -8.44) * mm, v(10.12, -8.5) * mm, v(9.22, -8.5) * mm]});
            skFitSpline(sketch, "E110.52", {"points": [v(11.99, -8.27) * mm, v(11.48, -8.39) * mm, v(10.8, -8.44) * mm]});
            skFitSpline(sketch, "E110.53", {"points": [v(12.87, -7.97) * mm, v(12.5, -8.15) * mm, v(11.99, -8.27) * mm]});
            skFitSpline(sketch, "E110.54", {"points": [v(13.52, -7.55) * mm, v(13.24, -7.8) * mm, v(12.87, -7.97) * mm]});
            skFitSpline(sketch, "E110.55", {"points": [v(14.02, -7) * mm, v(13.8, -7.31) * mm, v(13.52, -7.55) * mm]});
            skFitSpline(sketch, "E110.57", {"points": [v(14.46, -6.33) * mm, v(14.24, -6.7) * mm, v(14.02, -7) * mm]});
            skPoint(sketch, "E110.58", {"position": v(14.17, 5.1) * mm});
            skFitSpline(sketch, "E111.0", {"points": [v(-61.58, -3.6) * mm, v(-62.1, -2) * mm, v(-62.1, -0.05) * mm]});
            skFitSpline(sketch, "E111.1", {"points": [v(-60.03, -6.34) * mm, v(-61.05, -5.2) * mm, v(-61.58, -3.6) * mm]});
            skFitSpline(sketch, "E111.2", {"points": [v(-57.53, -8.1) * mm, v(-59.01, -7.49) * mm, v(-60.03, -6.34) * mm]});
            skFitSpline(sketch, "E111.3", {"points": [v(-54.12, -8.73) * mm, v(-56.05, -8.73) * mm, v(-57.53, -8.1) * mm]});
            skFitSpline(sketch, "E111.4", {"points": [v(-50.6, -8.1) * mm, v(-52.1, -8.73) * mm, v(-54.12, -8.73) * mm]});
            skFitSpline(sketch, "E111.5", {"points": [v(-46.62, -3.6) * mm, v(-47.11, -5.2) * mm, v(-48.1, -6.34) * mm]});
            skFitSpline(sketch, "E111.6", {"points": [v(-46.12, -0.03) * mm, v(-46.12, -1.98) * mm, v(-46.62, -3.6) * mm]});
            skFitSpline(sketch, "E111.7", {"points": [v(-46.62, 3.53) * mm, v(-46.12, 1.93) * mm, v(-46.12, -0.03) * mm]});
            skFitSpline(sketch, "E111.8", {"points": [v(-48.11, 6.26) * mm, v(-47.11, 5.13) * mm, v(-46.62, 3.53) * mm]});
            skFitSpline(sketch, "E111.9", {"points": [v(-50.61, 8) * mm, v(-49.1, 7.39) * mm, v(-48.11, 6.26) * mm]});
            skFitSpline(sketch, "E111.10", {"points": [v(-57.54, 8) * mm, v(-56.06, 8.62) * mm, v(-54.15, 8.62) * mm]});
            skFitSpline(sketch, "E111.11", {"points": [v(-61.58, 3.52) * mm, v(-61.05, 5.12) * mm, v(-60.04, 6.25) * mm]});
            skFitSpline(sketch, "E111.12", {"points": [v(-62.1, -0.05) * mm, v(-62.1, 1.92) * mm, v(-61.58, 3.52) * mm]});
            skFitSpline(sketch, "E111.13", {"points": [v(-60.04, 6.25) * mm, v(-59.02, 7.39) * mm, v(-57.54, 8) * mm]});
            skFitSpline(sketch, "E111.14", {"points": [v(-54.15, 8.62) * mm, v(-52.12, 8.62) * mm, v(-50.61, 8) * mm]});
            skFitSpline(sketch, "E111.15", {"points": [v(-50.3, 2.97) * mm, v(-50.53, 4.3) * mm, v(-51, 5.21) * mm]});
            skFitSpline(sketch, "E111.16", {"points": [v(-50.09, -0.05) * mm, v(-50.09, 1.65) * mm, v(-50.3, 2.97) * mm]});
            skFitSpline(sketch, "E111.17", {"points": [v(-50.3, -3.07) * mm, v(-50.09, -1.75) * mm, v(-50.09, -0.05) * mm]});
            skFitSpline(sketch, "E111.18", {"points": [v(-51, -5.31) * mm, v(-50.53, -4.4) * mm, v(-50.3, -3.07) * mm]});
            skFitSpline(sketch, "E111.19", {"points": [v(-52.26, -6.71) * mm, v(-51.5, -6.23) * mm, v(-51, -5.31) * mm]});
            skFitSpline(sketch, "E111.20", {"points": [v(-52.27, 6.6) * mm, v(-53.04, 7.09) * mm, v(-54.15, 7.09) * mm]});
            skFitSpline(sketch, "E111.21", {"points": [v(-51, 5.21) * mm, v(-51.5, 6.13) * mm, v(-52.27, 6.6) * mm]});
            skFitSpline(sketch, "E111.22", {"points": [v(-56, 6.6) * mm, v(-56.76, 6.13) * mm, v(-57.24, 5.21) * mm]});
            skFitSpline(sketch, "E111.23", {"points": [v(-54.15, 7.09) * mm, v(-55.24, 7.09) * mm, v(-56, 6.6) * mm]});
            skFitSpline(sketch, "E111.24", {"points": [v(-57.24, 5.21) * mm, v(-57.7, 4.3) * mm, v(-57.92, 2.97) * mm]});
            skFitSpline(sketch, "E111.25", {"points": [v(-57.92, 2.97) * mm, v(-58.13, 1.65) * mm, v(-58.13, -0.05) * mm]});
            skFitSpline(sketch, "E111.26", {"points": [v(-58.13, -0.05) * mm, v(-58.13, -1.75) * mm, v(-57.92, -3.07) * mm]});
            skFitSpline(sketch, "E111.27", {"points": [v(-57.92, -3.07) * mm, v(-57.7, -4.4) * mm, v(-57.24, -5.31) * mm]});
            skFitSpline(sketch, "E111.28", {"points": [v(-57.24, -5.31) * mm, v(-56.76, -6.23) * mm, v(-56, -6.71) * mm]});
            skFitSpline(sketch, "E111.29", {"points": [v(-56, -6.71) * mm, v(-55.23, -7.2) * mm, v(-54.12, -7.2) * mm]});
            skFitSpline(sketch, "E111.30", {"points": [v(-54.12, -7.2) * mm, v(-53.03, -7.2) * mm, v(-52.26, -6.71) * mm]});
            skFitSpline(sketch, "E111.31", {"points": [v(-48.1, -6.34) * mm, v(-49.1, -7.49) * mm, v(-50.6, -8.1) * mm]});
            skPoint(sketch, "E111.32", {"position": v(-49.25, -7.37) * mm});
            skSolve(sketch);
        }
        {
            var Q0;
            Q0=makeQuery(id+"F6.imprint","IMPRINT",FACE,{"disambiguationData":[TD([[makeQuery(id+"F6.imprint","IMPRINT",EDGE,{"derivedFrom":sQuery(id+"F6.wireOp",EDGE,"E33.0")}),-1.0]])]});
            var Q1;
            Q1=makeQuery(id+"F6.imprint","IMPRINT",FACE,{"disambiguationData":[TD([[makeQuery(id+"F6.imprint","IMPRINT",EDGE,{"derivedFrom":sQuery(id+"F6.wireOp",EDGE,"E106.0")}),-1.0]])]});
            var Q2;
            Q2=makeQuery(id+"F6.imprint","IMPRINT",FACE,{"disambiguationData":[TD([[makeQuery(id+"F6.imprint","IMPRINT",EDGE,{"derivedFrom":sQuery(id+"F6.wireOp",EDGE,"E64.0")}),-1.0]])]});
            var Q3;
            Q3=makeQuery(id+"F6.imprint","IMPRINT",FACE,{"disambiguationData":[TD([[makeQuery(id+"F6.imprint","IMPRINT",EDGE,{"derivedFrom":sQuery(id+"F6.wireOp",EDGE,"E111.0")}),-1.0]])]});
            var Q4;
            Q4=makeQuery(id+"F6.imprint","IMPRINT",FACE,{"disambiguationData":[TD([[makeQuery(id+"F6.imprint","IMPRINT",EDGE,{"derivedFrom":makeQuery(id+"F3.boolean.opBoolean","COPY",EDGE,{"derivedFrom":makeQuery(id+"F3.opExtrude","CAP_EDGE",EDGE,{"disambiguationData":[OSD([sQuery(id+"F2.wireOp",EDGE,"E1.sketch_text.stroke-368")])],"isStart":false})})}),-1.0]])]});
            var Q5;
            Q5=makeQuery(id+"F6.imprint","IMPRINT",FACE,{"disambiguationData":[TD([[makeQuery(id+"F6.imprint","IMPRINT",EDGE,{"derivedFrom":makeQuery(id+"F3.boolean.opBoolean","COPY",EDGE,{"derivedFrom":makeQuery(id+"F3.opExtrude","CAP_EDGE",EDGE,{"disambiguationData":[OSD([sQuery(id+"F2.wireOp",EDGE,"E1.sketch_text.stroke-223")])],"isStart":false})})}),-1.0]])]});
            var Q6;
            Q6=makeQuery(id+"F6.imprint","IMPRINT",FACE,{"disambiguationData":[TD([[makeQuery(id+"F6.imprint","IMPRINT",EDGE,{"derivedFrom":sQuery(id+"F6.wireOp",EDGE,"E109.0")}),-1.0]])]});
            var Q7;
            Q7=makeQuery(id+"F6.imprint","IMPRINT",FACE,{"disambiguationData":[TD([[makeQuery(id+"F6.imprint","IMPRINT",EDGE,{"derivedFrom":makeQuery(id+"F3.boolean.opBoolean","COPY",EDGE,{"derivedFrom":makeQuery(id+"F3.opExtrude","CAP_EDGE",EDGE,{"disambiguationData":[OSD([sQuery(id+"F2.wireOp",EDGE,"E1.sketch_text.stroke-276")])],"isStart":false})})}),-1.0]])]});
            var Q8;
            Q8=makeQuery(id+"F6.imprint","IMPRINT",FACE,{"disambiguationData":[TD([[makeQuery(id+"F6.imprint","IMPRINT",EDGE,{"derivedFrom":sQuery(id+"F6.wireOp",EDGE,"E61.0")}),-1.0]])]});
            var Q9;
            Q9=makeQuery(id+"F6.imprint","IMPRINT",FACE,{"disambiguationData":[TD([[makeQuery(id+"F6.imprint","IMPRINT",EDGE,{"derivedFrom":sQuery(id+"F6.wireOp",EDGE,"E4.0")}),-1.0]])]});
            extrude(context, id + "F7", {"entities" : qUnion([Q0, Q1, Q2, Q3, Q4, Q5, Q6, Q7, Q8, Q9]), "operationType" : NewBodyOperationType.REMOVE, "oppositeDirection" : true, "depth" : 3.2 * mm, "offsetDistance" : 25 * mm});
        }
        {
            var Q0;
            {var subQ0=sQuery(id+"F0.wireOp",EDGE,"E0.left");var subQ1=sQuery(id+"F0.wireOp",EDGE,"E0.bottom");var subQ2=sQuery(id+"F0.wireOp",EDGE,"E0.right");var subQ3=sQuery(id+"F0.wireOp",EDGE,"E0.top");Q0=makeQuery(id+"F3.boolean.opBoolean","SPLIT",FACE,{"disambiguationData":[TD([makeQuery(id+"F1.opExtrude","SWEPT_FACE",FACE,{"disambiguationData":[OSD([subQ1])]})])],"derivedFrom":makeQuery(id+"F1.opExtrude","CAP_FACE",FACE,{"disambiguationData":[OSD([subQ1,subQ3,subQ0,subQ2])],"isStart":true})});}
            var sketch = newSketch(context, id + "F8", { "sketchPlane" : qUnion([Q0])});
            skLineSegment(sketch, "E112.0.0", {"start": v(-105, -10) * mm, "end": v(105, -10) * mm});
            skLineSegment(sketch, "E112.0.1", {"start": v(105, -10) * mm, "end": v(105, 10) * mm});
            skLineSegment(sketch, "E112.0.2", {"start": v(105, 10) * mm, "end": v(-105, 10) * mm});
            skLineSegment(sketch, "E112.0.3", {"start": v(-105, 10) * mm, "end": v(-105, -10) * mm});
            skSolve(sketch);
        }
        {
            var Q0;
            Q0 = qSketchRegion(id + "F8", true);
            extrude(context, id + "F9", {"entities" : qUnion([Q0]), "operationType" : NewBodyOperationType.ADD, "depth" : 5 * mm, "offsetDistance" : 25 * mm});
        }
        {
            var Q0;
            Q0=makeQuery(id+"F5.opExtrude","CAP_FACE",FACE,{"disambiguationData":[OSD([sQuery(id+"F4.wireOp",EDGE,"E3.bottom"),sQuery(id+"F4.wireOp",EDGE,"E3.top"),sQuery(id+"F4.wireOp",EDGE,"E3.left"),sQuery(id+"F4.wireOp",EDGE,"E3.right")])],"isStart":false});
            var sketch = newSketch(context, id + "F10", { "sketchPlane" : qUnion([Q0])});
            skCircle(sketch, "E113", {"center": v(-100, 0) * mm, "radius": 2.62 * mm});
            skCircle(sketch, "E114", {"center": v(100, 0) * mm, "radius": 2.63 * mm});
            skSolve(sketch);
        }
        {
            var Q0;
            Q0 = qSketchRegion(id + "F10", true);
            extrude(context, id + "F11", {"entities" : qUnion([Q0]), "operationType" : NewBodyOperationType.REMOVE, "oppositeDirection" : true, "depth" : 25 * mm, "offsetDistance" : 25 * mm});
        }
        {
            var Q0;
            Q0=makeQuery(id+"F5.opExtrude","CAP_FACE",FACE,{"disambiguationData":[OSD([sQuery(id+"F4.wireOp",EDGE,"E3.bottom"),sQuery(id+"F4.wireOp",EDGE,"E3.top"),sQuery(id+"F4.wireOp",EDGE,"E3.left"),sQuery(id+"F4.wireOp",EDGE,"E3.right")])],"isStart":false});
            var sketch = newSketch(context, id + "F12", { "sketchPlane" : qUnion([Q0])});
            skCircle(sketch, "E115", {"center": v(-100, 0) * mm, "radius": 3.75 * mm});
            skCircle(sketch, "E116", {"center": v(100, 0) * mm, "radius": 3.75 * mm});
            skSolve(sketch);
        }
        {
            var Q0;
            Q0 = qSketchRegion(id + "F12", true);
            var Q1;
            {var subQ0=sQuery(id+"F0.wireOp",EDGE,"E0.left");var subQ1=sQuery(id+"F0.wireOp",EDGE,"E0.bottom");var subQ2=sQuery(id+"F0.wireOp",EDGE,"E0.right");var subQ3=sQuery(id+"F0.wireOp",EDGE,"E0.top");Q1=makeQuery(id+"F3.boolean.opBoolean","SPLIT",FACE,{"disambiguationData":[TD([makeQuery(id+"F1.opExtrude","SWEPT_FACE",FACE,{"disambiguationData":[OSD([subQ1])]})])],"derivedFrom":makeQuery(id+"F1.opExtrude","CAP_FACE",FACE,{"disambiguationData":[OSD([subQ1,subQ3,subQ0,subQ2])],"isStart":false})});}
            extrude(context, id + "F13", {"entities" : qUnion([Q0]), "operationType" : NewBodyOperationType.REMOVE, "endBound" : BoundingType.UP_TO_SURFACE, "oppositeDirection" : true, "depth" : 25 * mm, "endBoundEntityFace" : qUnion([Q1]), "offsetDistance" : 25 * mm});
        }
        {
            var Q0;
            Q0=makeQuery(id+"F9.boolean.opBoolean","MERGE",FACE,{"derivedFrom":[makeQuery(id+"F1.opExtrude","SWEPT_FACE",FACE,{"disambiguationData":[OSD([sQuery(id+"F0.wireOp",EDGE,"E0.right")])]}),makeQuery(id+"F9.opExtrude","SWEPT_FACE",FACE,{"disambiguationData":[OSD([sQuery(id+"F8.wireOp",EDGE,"E112.0.1")])]})]});
            var sketch = newSketch(context, id + "F14", { "sketchPlane" : qUnion([Q0])});
            skLineSegment(sketch, "E117.bottom", {"start": v(-4, 5.5) * mm, "end": v(1, 5.5) * mm});
            skLineSegment(sketch, "E117.top", {"start": v(-4, -5.5) * mm, "end": v(1, -5.5) * mm});
            skLineSegment(sketch, "E117.left", {"start": v(-4, 5.5) * mm, "end": v(-4, -5.5) * mm});
            skLineSegment(sketch, "E117.right", {"start": v(1, 5.5) * mm, "end": v(1, -5.5) * mm});
            skLineSegment(sketch, "E118", {"start": v(-4, 0) * mm, "end": v(1, 0) * mm, "construction": true});
            skSolve(sketch);
        }
        {
            var Q0;
            Q0 = qSketchRegion(id + "F14", true);
            extrude(context, id + "F15", {"entities" : qUnion([Q0]), "operationType" : NewBodyOperationType.REMOVE, "endBound" : BoundingType.THROUGH_ALL, "oppositeDirection" : true, "depth" : 25 * mm, "offsetDistance" : 25 * mm});
        }
        {
            var Q0;
            Q0=makeQuery(id+"F9.opExtrude","CAP_FACE",FACE,{"disambiguationData":[OSD([sQuery(id+"F8.wireOp",EDGE,"E112.0.0"),sQuery(id+"F8.wireOp",EDGE,"E112.0.1"),sQuery(id+"F8.wireOp",EDGE,"E112.0.2"),sQuery(id+"F8.wireOp",EDGE,"E112.0.3")])],"isStart":false});
            var sketch = newSketch(context, id + "F16", { "sketchPlane" : qUnion([Q0])});
            skLineSegment(sketch, "E119.bottom", {"start": v(105, 10) * mm, "end": v(-20, 10) * mm});
            skLineSegment(sketch, "E119.top", {"start": v(105, -10) * mm, "end": v(-20, -10) * mm});
            skLineSegment(sketch, "E119.left", {"start": v(105, 10) * mm, "end": v(105, -10) * mm});
            skLineSegment(sketch, "E119.right", {"start": v(-20, 10) * mm, "end": v(-20, -10) * mm});
            skSolve(sketch);
        }
        {
            var Q0;
            Q0 = qSketchRegion(id + "F16", true);
            extrude(context, id + "F17", {"entities" : qUnion([Q0]), "operationType" : NewBodyOperationType.REMOVE, "oppositeDirection" : true, "depth" : 25 * mm, "offsetDistance" : 25 * mm});
        }
    });
